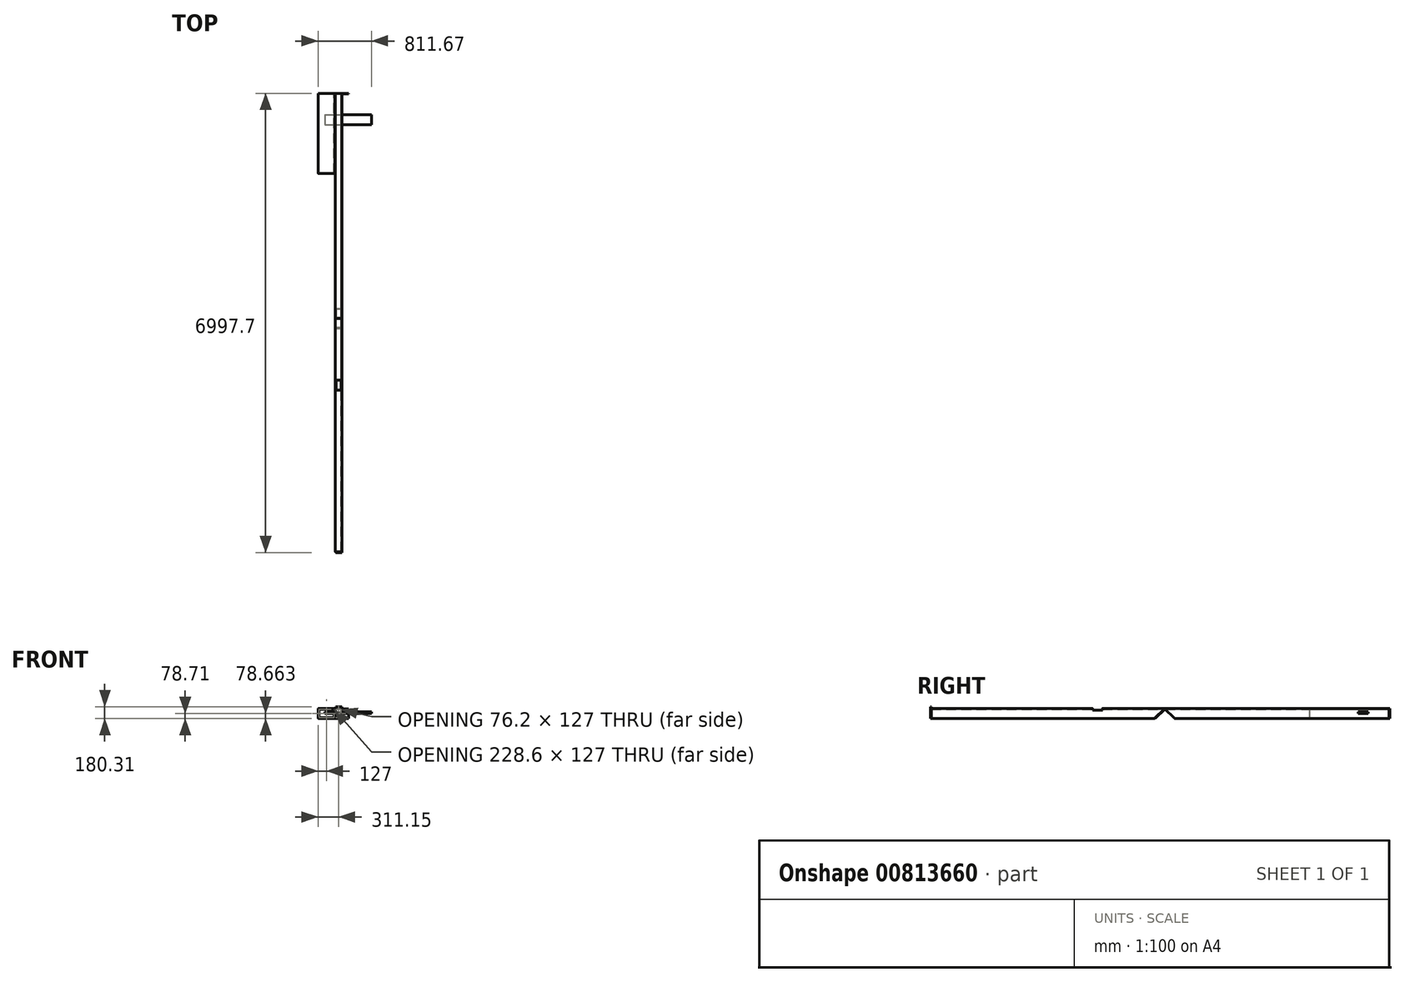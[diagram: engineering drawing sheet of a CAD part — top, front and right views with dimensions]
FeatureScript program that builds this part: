
annotation { "Feature Type Name" : "Feature", "Feature Type Description" : "" }
export const myFeature = defineFeature(function(context is Context, id is Id, definition is map)
    precondition{}
    {
        {
            var Q0;
            Q0=qCreatedBy(makeId("Front.planeOp"),FACE);
            var sketch = newSketch(context, id + "F0", { "sketchPlane" : qUnion([Q0])});
            skLineSegment(sketch, "E0.bottom", {"start": v(50.8, -76.2) * mm, "end": v(-50.8, -76.2) * mm});
            skLineSegment(sketch, "E0.top", {"start": v(50.8, 76.2) * mm, "end": v(-50.8, 76.2) * mm});
            skLineSegment(sketch, "E0.left", {"start": v(50.8, -76.2) * mm, "end": v(50.8, 76.2) * mm});
            skLineSegment(sketch, "E0.right", {"start": v(-50.8, -76.2) * mm, "end": v(-50.8, 76.2) * mm});
            skPoint(sketch, "E0.middle", {"position": v(0, 0) * mm});
            skLineSegment(sketch, "E1.0", {"start": v(38.1, 63.5) * mm, "end": v(-38.1, 63.5) * mm});
            skLineSegment(sketch, "E1.1", {"start": v(38.1, -63.5) * mm, "end": v(38.1, 63.5) * mm});
            skLineSegment(sketch, "E1.2", {"start": v(38.1, -63.5) * mm, "end": v(-38.1, -63.5) * mm});
            skLineSegment(sketch, "E1.3", {"start": v(-38.1, -63.5) * mm, "end": v(-38.1, 63.5) * mm});
            skSolve(sketch);
        }
        {
            var Q0;
            Q0=qCreatedBy(makeId("Front.planeOp"),FACE);
            var sketch = newSketch(context, id + "F1", { "sketchPlane" : qUnion([Q0])});
            skLineSegment(sketch, "E2.bottom", {"start": v(-57.15, -76.25) * mm, "end": v(-311.15, -76.25) * mm});
            skLineSegment(sketch, "E2.top", {"start": v(-57.15, 76.15) * mm, "end": v(-311.15, 76.15) * mm});
            skLineSegment(sketch, "E2.left", {"start": v(-57.15, -76.25) * mm, "end": v(-57.15, 76.15) * mm});
            skLineSegment(sketch, "E2.right", {"start": v(-311.15, -76.25) * mm, "end": v(-311.15, 76.15) * mm});
            skLineSegment(sketch, "E3.0", {"start": v(-298.45, -63.55) * mm, "end": v(-298.45, 63.45) * mm});
            skLineSegment(sketch, "E3.1", {"start": v(-69.85, -63.55) * mm, "end": v(-298.45, -63.55) * mm});
            skLineSegment(sketch, "E3.2", {"start": v(-69.85, -63.55) * mm, "end": v(-69.85, 63.45) * mm});
            skLineSegment(sketch, "E3.3", {"start": v(-69.85, 63.45) * mm, "end": v(-298.45, 63.45) * mm});
            skSolve(sketch);
        }
        {
            var Q0;
            Q0=qCreatedBy(makeId("Front.planeOp"),FACE);
            var sketch = newSketch(context, id + "F2", { "sketchPlane" : qUnion([Q0])});
            skLineSegment(sketch, "E4.bottom", {"start": v(59.44, 69.57) * mm, "end": v(154.69, 69.57) * mm});
            skLineSegment(sketch, "E4.top", {"start": v(59.44, -76.48) * mm, "end": v(154.69, -76.48) * mm});
            skLineSegment(sketch, "E4.left", {"start": v(59.44, 69.57) * mm, "end": v(59.44, -76.48) * mm});
            skLineSegment(sketch, "E4.right", {"start": v(154.69, 69.57) * mm, "end": v(154.69, -76.48) * mm});
            skSolve(sketch);
        }
        {
            var Q0;
            Q0=makeQuery(id+"F1.imprint","IMPRINT",FACE,{"disambiguationData":[TD([[makeQuery(id+"F1.imprint","IMPRINT",EDGE,{"derivedFrom":sQuery(id+"F1.wireOp",EDGE,"E2.bottom")}),-1.0]])]});
            extrude(context, id + "F3", {"entities" : qUnion([Q0]), "depth" : 1219.2 * mm});
        }
        {
            var Q0;
            Q0=makeQuery(id+"F0.imprint","IMPRINT",FACE,{"disambiguationData":[TD([[makeQuery(id+"F0.imprint","IMPRINT",EDGE,{"derivedFrom":sQuery(id+"F0.wireOp",EDGE,"E0.bottom")}),-1.0]])]});
            extrude(context, id + "F4", {"entities" : qUnion([Q0]), "depth" : 3429 * mm});
        }
        {
            var Q0;
            Q0=makeQuery(id+"F2.imprint","IMPRINT",FACE,{"disambiguationData":[TD([[makeQuery(id+"F2.imprint","IMPRINT",EDGE,{"derivedFrom":sQuery(id+"F2.wireOp",EDGE,"E4.bottom")}),-1.0]])]});
            extrude(context, id + "F5", {"entities" : qUnion([Q0]), "depth" : 9.52 * mm});
        }
        {
            var Q0;
            Q0=makeQuery(id+"F4.opExtrude","CAP_FACE",FACE,{"disambiguationData":[OSD([sQuery(id+"F0.wireOp",EDGE,"E0.bottom"),sQuery(id+"F0.wireOp",EDGE,"E0.top"),sQuery(id+"F0.wireOp",EDGE,"E0.left"),sQuery(id+"F0.wireOp",EDGE,"E0.right"),sQuery(id+"F0.wireOp",EDGE,"E1.0"),sQuery(id+"F0.wireOp",EDGE,"E1.1"),sQuery(id+"F0.wireOp",EDGE,"E1.2"),sQuery(id+"F0.wireOp",EDGE,"E1.3")])],"isStart":false});
            extrude(context, id + "F6", {"entities" : qUnion([Q0]), "depth" : 3556 * mm});
        }
        {
            var Q0;
            Q0=makeQuery(id+"F6.opExtrude","SWEPT_FACE",FACE,{"disambiguationData":[OSD([sQuery(id+"F0.wireOp",EDGE,"E0.left")])]});
            var sketch = newSketch(context, id + "F7", { "sketchPlane" : qUnion([Q0])});
            skLineSegment(sketch, "E5", {"start": v(-3429, 76.2) * mm, "end": v(-3581.4, -76.2) * mm});
            skSolve(sketch);
        }
        {
            var Q0;
            Q0=makeQuery(id+"F4.opExtrude","SWEPT_FACE",FACE,{"disambiguationData":[OSD([sQuery(id+"F0.wireOp",EDGE,"E0.left")])]});
            var sketch = newSketch(context, id + "F8", { "sketchPlane" : qUnion([Q0])});
            skLineSegment(sketch, "E6", {"start": v(-3429, 76.2) * mm, "end": v(-3276.6, -76.2) * mm});
            skSolve(sketch);
        }
        {
            var Q0;
            Q0=qSketchRegion(id+"F8",true);
            var Q1;
            {var subQ0=sQuery(id+"F8.wireOp",EDGE,"E6");Q1=makeQuery(id+"F8.imprint","IMPRINT",FACE,{"disambiguationData":[TD([[makeQuery(id+"F8.imprint","IMPRINT",EDGE,{"derivedFrom":subQ0}),-1.0]])]});}
            extrude(context, id + "F9", {"entities" : qUnion([Q0, Q1]), "operationType" : NewBodyOperationType.REMOVE, "endBound" : BoundingType.THROUGH_ALL, "oppositeDirection" : true, "depth" : 25.4 * mm});
        }
        {
            var Q0;
            {var subQ0=sQuery(id+"F7.wireOp",EDGE,"E5");Q0=makeQuery(id+"F7.imprint","IMPRINT",FACE,{"disambiguationData":[TD([[makeQuery(id+"F7.imprint","IMPRINT",EDGE,{"derivedFrom":subQ0}),1.0]])]});}
            extrude(context, id + "F10", {"entities" : qUnion([Q0]), "operationType" : NewBodyOperationType.REMOVE, "endBound" : BoundingType.THROUGH_ALL, "oppositeDirection" : true, "depth" : 25.4 * mm});
        }
        {
            var Q0;
            Q0=makeQuery(id+"F10.boolean.opBoolean","COPY",FACE,{"derivedFrom":makeQuery(id+"F10.opExtrude","SWEPT_FACE",FACE,{"disambiguationData":[OSD([sQuery(id+"F7.wireOp",EDGE,"E5")])]})});
            var sketch = newSketch(context, id + "F11", { "sketchPlane" : qUnion([Q0])});
            skLineSegment(sketch, "E7", {"start": v(-44.45, -2580.34) * mm, "end": v(-44.45, -2370.79) * mm});
            skLineSegment(sketch, "E8", {"start": v(-44.45, -2370.79) * mm, "end": v(50.8, -2370.79) * mm});
            skLineSegment(sketch, "E9", {"start": v(50.8, -2370.79) * mm, "end": v(50.8, -2580.34) * mm});
            skLineSegment(sketch, "E10", {"start": v(50.8, -2580.34) * mm, "end": v(-44.45, -2580.34) * mm});
            skSolve(sketch);
        }
        {
            var Q0;
            Q0=makeQuery(id+"F11.imprint","IMPRINT",FACE,{"disambiguationData":[TD([[makeQuery(id+"F11.imprint","IMPRINT",EDGE,{"derivedFrom":sQuery(id+"F11.wireOp",EDGE,"E7")}),-1.0]])]});
            var Q1;
            {var subQ0=makeQuery(id+"F10.opExtrude","SWEPT_FACE",FACE,{"disambiguationData":[OSD([sQuery(id+"F7.wireOp",EDGE,"E5")])]});Q1=makeQuery(id+"F11.imprint","IMPRINT",FACE,{"disambiguationData":[TD([[makeQuery(id+"F11.imprint","IMPRINT",EDGE,{"derivedFrom":makeQuery(id+"F10.boolean.opBoolean","INTERSECT",EDGE,{"derivedFrom":[makeQuery(id+"F6.opExtrude","SWEPT_FACE",FACE,{"disambiguationData":[OSD([sQuery(id+"F0.wireOp",EDGE,"E1.0")])]}),subQ0]})}),-1.0]])]});}
            extrude(context, id + "F12", {"entities" : qUnion([Q0, Q1]), "depth" : 9.52 * mm});
        }
        {
            var Q0;
            Q0=makeQuery(id+"F6.opExtrude","CAP_FACE",FACE,{"disambiguationData":[OSD([sQuery(id+"F0.wireOp",EDGE,"E0.bottom"),sQuery(id+"F0.wireOp",EDGE,"E0.top"),sQuery(id+"F0.wireOp",EDGE,"E0.left"),sQuery(id+"F0.wireOp",EDGE,"E0.right"),sQuery(id+"F0.wireOp",EDGE,"E1.0"),sQuery(id+"F0.wireOp",EDGE,"E1.1"),sQuery(id+"F0.wireOp",EDGE,"E1.2"),sQuery(id+"F0.wireOp",EDGE,"E1.3")])],"isStart":false});
            var sketch = newSketch(context, id + "F13", { "sketchPlane" : qUnion([Q0])});
            skLineSegment(sketch, "E11.bottom", {"start": v(50.8, -76.2) * mm, "end": v(-44.45, -76.2) * mm});
            skLineSegment(sketch, "E11.left", {"start": v(50.8, -76.2) * mm, "end": v(50.8, 101.6) * mm});
            skLineSegment(sketch, "E11.right", {"start": v(-44.45, -76.2) * mm, "end": v(-44.45, 101.6) * mm});
            skPoint(sketch, "E11.middle", {"position": v(0, 0) * mm});
            skLineSegment(sketch, "E12", {"start": v(-44.45, 101.6) * mm, "end": v(50.8, 101.6) * mm});
            skSolve(sketch);
        }
        {
            var Q0;
            {var subQ2=sQuery(id+"F13.wireOp",EDGE,"E11.bottom");Q0=makeQuery(id+"F13.imprint","IMPRINT",FACE,{"disambiguationData":[TD([[makeQuery(id+"F13.imprint","IMPRINT",EDGE,{"derivedFrom":subQ2}),-1.0]])]});}
            var Q1;
            Q1=makeQuery(id+"F13.imprint","IMPRINT",FACE,{"disambiguationData":[TD([[makeQuery(id+"F13.imprint","IMPRINT",EDGE,{"derivedFrom":makeQuery(id+"F6.opExtrude","CAP_EDGE",EDGE,{"disambiguationData":[OSD([sQuery(id+"F0.wireOp",EDGE,"E1.0")])],"isStart":false})}),1.0]])]});
            var Q2;
            {var subQ2=sQuery(id+"F13.wireOp",EDGE,"E12");Q2=makeQuery(id+"F13.imprint","IMPRINT",FACE,{"disambiguationData":[TD([[makeQuery(id+"F13.imprint","IMPRINT",EDGE,{"derivedFrom":subQ2}),-1.0]])]});}
            extrude(context, id + "F14", {"entities" : qUnion([Q0, Q1, Q2]), "depth" : 12.7 * mm});
        }
        {
            var Q0;
            Q0=makeQuery(id+"F4.opExtrude","SWEPT_EDGE",EDGE,{"disambiguationData":[OSD([sQuery(id+"F0.wireOp",EDGE,"E0.top"),sQuery(id+"F0.wireOp",EDGE,"E0.right")])]});
            var Q1;
            Q1=makeQuery(id+"F4.opExtrude","SWEPT_EDGE",EDGE,{"disambiguationData":[OSD([sQuery(id+"F0.wireOp",EDGE,"E0.bottom"),sQuery(id+"F0.wireOp",EDGE,"E0.right")])]});
            var Q2;
            Q2=makeQuery(id+"F4.opExtrude","SWEPT_EDGE",EDGE,{"disambiguationData":[OSD([sQuery(id+"F0.wireOp",EDGE,"E0.bottom"),sQuery(id+"F0.wireOp",EDGE,"E0.left")])]});
            var Q3;
            Q3=makeQuery(id+"F4.opExtrude","SWEPT_EDGE",EDGE,{"disambiguationData":[OSD([sQuery(id+"F0.wireOp",EDGE,"E0.top"),sQuery(id+"F0.wireOp",EDGE,"E0.left")])]});
            var Q4;
            Q4=makeQuery(id+"F4.opExtrude","SWEPT_EDGE",EDGE,{"disambiguationData":[OSD([sQuery(id+"F0.wireOp",EDGE,"E1.0"),sQuery(id+"F0.wireOp",EDGE,"E1.3")])]});
            var Q5;
            Q5=makeQuery(id+"F4.opExtrude","SWEPT_EDGE",EDGE,{"disambiguationData":[OSD([sQuery(id+"F0.wireOp",EDGE,"E1.0"),sQuery(id+"F0.wireOp",EDGE,"E1.1")])]});
            var Q6;
            Q6=makeQuery(id+"F4.opExtrude","SWEPT_EDGE",EDGE,{"disambiguationData":[OSD([sQuery(id+"F0.wireOp",EDGE,"E1.1"),sQuery(id+"F0.wireOp",EDGE,"E1.2")])]});
            var Q7;
            Q7=makeQuery(id+"F4.opExtrude","SWEPT_EDGE",EDGE,{"disambiguationData":[OSD([sQuery(id+"F0.wireOp",EDGE,"E1.2"),sQuery(id+"F0.wireOp",EDGE,"E1.3")])]});
            var Q8;
            Q8=makeQuery(id+"F6.opExtrude","SWEPT_EDGE",EDGE,{"disambiguationData":[OSD([sQuery(id+"F0.wireOp",EDGE,"E0.bottom"),sQuery(id+"F0.wireOp",EDGE,"E0.left")])]});
            var Q9;
            Q9=makeQuery(id+"F6.opExtrude","SWEPT_EDGE",EDGE,{"disambiguationData":[OSD([sQuery(id+"F0.wireOp",EDGE,"E0.bottom"),sQuery(id+"F0.wireOp",EDGE,"E0.right")])]});
            var Q10;
            Q10=makeQuery(id+"F6.opExtrude","SWEPT_EDGE",EDGE,{"disambiguationData":[OSD([sQuery(id+"F0.wireOp",EDGE,"E0.top"),sQuery(id+"F0.wireOp",EDGE,"E0.left")])]});
            var Q11;
            Q11=makeQuery(id+"F6.opExtrude","SWEPT_EDGE",EDGE,{"disambiguationData":[OSD([sQuery(id+"F0.wireOp",EDGE,"E0.top"),sQuery(id+"F0.wireOp",EDGE,"E0.right")])]});
            var Q12;
            Q12=makeQuery(id+"F6.opExtrude","SWEPT_EDGE",EDGE,{"disambiguationData":[OSD([sQuery(id+"F0.wireOp",EDGE,"E1.0"),sQuery(id+"F0.wireOp",EDGE,"E1.3")])]});
            var Q13;
            Q13=makeQuery(id+"F6.opExtrude","SWEPT_EDGE",EDGE,{"disambiguationData":[OSD([sQuery(id+"F0.wireOp",EDGE,"E1.0"),sQuery(id+"F0.wireOp",EDGE,"E1.1")])]});
            var Q14;
            Q14=makeQuery(id+"F6.opExtrude","SWEPT_EDGE",EDGE,{"disambiguationData":[OSD([sQuery(id+"F0.wireOp",EDGE,"E1.1"),sQuery(id+"F0.wireOp",EDGE,"E1.2")])]});
            var Q15;
            Q15=makeQuery(id+"F6.opExtrude","SWEPT_EDGE",EDGE,{"disambiguationData":[OSD([sQuery(id+"F0.wireOp",EDGE,"E1.2"),sQuery(id+"F0.wireOp",EDGE,"E1.3")])]});
            var Q16;
            Q16=makeQuery(id+"F3.opExtrude","SWEPT_EDGE",EDGE,{"disambiguationData":[OSD([sQuery(id+"F1.wireOp",EDGE,"E3.2"),sQuery(id+"F1.wireOp",EDGE,"E3.3")])]});
            var Q17;
            Q17=makeQuery(id+"F3.opExtrude","SWEPT_EDGE",EDGE,{"disambiguationData":[OSD([sQuery(id+"F1.wireOp",EDGE,"E3.1"),sQuery(id+"F1.wireOp",EDGE,"E3.2")])]});
            var Q18;
            Q18=makeQuery(id+"F3.opExtrude","SWEPT_EDGE",EDGE,{"disambiguationData":[OSD([sQuery(id+"F1.wireOp",EDGE,"E3.0"),sQuery(id+"F1.wireOp",EDGE,"E3.1")])]});
            var Q19;
            Q19=makeQuery(id+"F3.opExtrude","SWEPT_EDGE",EDGE,{"disambiguationData":[OSD([sQuery(id+"F1.wireOp",EDGE,"E3.0"),sQuery(id+"F1.wireOp",EDGE,"E3.3")])]});
            var Q20;
            Q20=makeQuery(id+"F3.opExtrude","SWEPT_EDGE",EDGE,{"disambiguationData":[OSD([sQuery(id+"F1.wireOp",EDGE,"E2.bottom"),sQuery(id+"F1.wireOp",EDGE,"E2.left")])]});
            var Q21;
            Q21=makeQuery(id+"F3.opExtrude","SWEPT_EDGE",EDGE,{"disambiguationData":[OSD([sQuery(id+"F1.wireOp",EDGE,"E2.bottom"),sQuery(id+"F1.wireOp",EDGE,"E2.right")])]});
            var Q22;
            Q22=makeQuery(id+"F3.opExtrude","SWEPT_EDGE",EDGE,{"disambiguationData":[OSD([sQuery(id+"F1.wireOp",EDGE,"E2.top"),sQuery(id+"F1.wireOp",EDGE,"E2.right")])]});
            var Q23;
            Q23=makeQuery(id+"F3.opExtrude","SWEPT_EDGE",EDGE,{"disambiguationData":[OSD([sQuery(id+"F1.wireOp",EDGE,"E2.top"),sQuery(id+"F1.wireOp",EDGE,"E2.left")])]});
            fillet(context, id + "F15", {"entities" : qUnion([Q0, Q1, Q2, Q3, Q4, Q5, Q6, Q7, Q8, Q9, Q10, Q11, Q12, Q13, Q14, Q15, Q16, Q17, Q18, Q19, Q20, Q21, Q22, Q23]), "radius" : 5.08 * mm, "tangentPropagation" : true, "allowEdgeOverflow" : false});
        }
        {
            var Q0;
            Q0=qCreatedBy(makeId("Top.planeOp"),FACE);
            var sketch = newSketch(context, id + "F16", { "sketchPlane" : qUnion([Q0])});
            skLineSegment(sketch, "E13.bottom", {"start": v(-210.68, -326.94) * mm, "end": v(500.52, -326.94) * mm});
            skLineSegment(sketch, "E13.top", {"start": v(-210.68, -479.34) * mm, "end": v(500.52, -479.34) * mm});
            skLineSegment(sketch, "E13.left", {"start": v(-210.68, -326.94) * mm, "end": v(-210.68, -479.34) * mm});
            skLineSegment(sketch, "E13.right", {"start": v(500.52, -326.94) * mm, "end": v(500.52, -479.34) * mm});
            skSolve(sketch);
        }
        {
            var Q0;
            Q0=qSketchRegion(id+"F16",true);
            extrude(context, id + "F17", {"entities" : qUnion([Q0]), "depth" : 25.4 * mm});
        }
        {
            var Q0;
            Q0=makeQuery(id+"F6.opExtrude","SWEPT_FACE",FACE,{"disambiguationData":[OSD([sQuery(id+"F0.wireOp",EDGE,"E0.top")])]});
            var sketch = newSketch(context, id + "F18", { "sketchPlane" : qUnion([Q0])});
            skLineSegment(sketch, "E14", {"start": v(117.98, -4373.88) * mm, "end": v(-129, -4373.88) * mm});
            skLineSegment(sketch, "E15", {"start": v(117.98, -4373.88) * mm, "end": v(117.98, -4526.28) * mm});
            skLineSegment(sketch, "E16", {"start": v(117.98, -4526.28) * mm, "end": v(-129, -4526.28) * mm});
            skLineSegment(sketch, "E17", {"start": v(-129, -4526.28) * mm, "end": v(-129, -4373.88) * mm});
            skSolve(sketch);
        }
        {
            var Q0;
            Q0=qSketchRegion(id+"F18",true);
            extrude(context, id + "F19", {"entities" : qUnion([Q0]), "operationType" : NewBodyOperationType.REMOVE, "oppositeDirection" : true, "depth" : 25.4 * mm});
        }
    });
